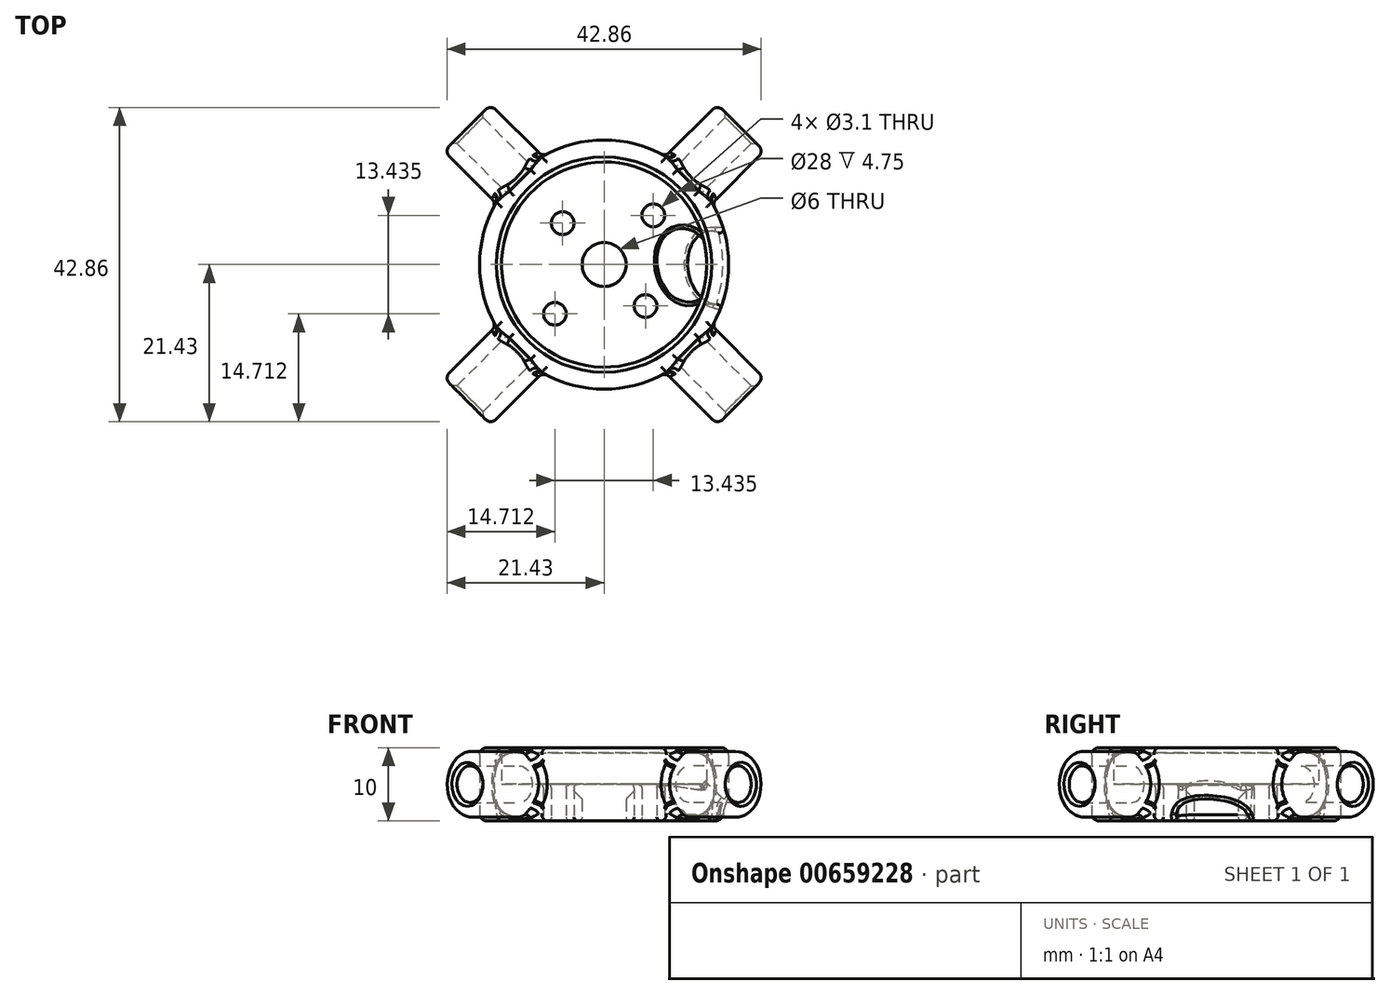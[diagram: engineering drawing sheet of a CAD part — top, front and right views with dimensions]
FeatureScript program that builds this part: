
annotation { "Feature Type Name" : "Feature", "Feature Type Description" : "" }
export const myFeature = defineFeature(function(context is Context, id is Id, definition is map)
    precondition{}
    {
        {
            var Q0;
            Q0=qCreatedBy(makeId("Top.planeOp"),FACE);
            var sketch = newSketch(context, id + "F0", { "sketchPlane" : qUnion([Q0])});
            skCircle(sketch, "E0", {"center": v(0, 0) * mm, "radius": 14 * mm});
            skCircle(sketch, "E1", {"center": v(0, 0) * mm, "radius": 17 * mm});
            skCircle(sketch, "E2", {"center": v(-9.5, 0) * mm, "radius": 1.55 * mm});
            skCircle(sketch, "E3", {"center": v(0, 8) * mm, "radius": 1.55 * mm});
            skCircle(sketch, "E4", {"center": v(9.5, 0) * mm, "radius": 1.55 * mm});
            skCircle(sketch, "E5", {"center": v(0, -8) * mm, "radius": 1.55 * mm});
            skCircle(sketch, "E6", {"center": v(0, 0) * mm, "radius": 3 * mm});
            skLineSegment(sketch, "E7", {"start": v(-16.4, 4.5) * mm, "end": v(-16.4, -4.5) * mm});
            skLineSegment(sketch, "E8", {"start": v(16.4, 4.5) * mm, "end": v(16.4, -4.5) * mm});
            skLineSegment(sketch, "E9", {"start": v(-4.5, 16.4) * mm, "end": v(4.5, 16.4) * mm});
            skLineSegment(sketch, "E10", {"start": v(-4.5, -16.4) * mm, "end": v(4.5, -16.4) * mm});
            skSolve(sketch);
        }
        {
            var Q0;
            Q0=makeQuery(id+"F0.imprint","IMPRINT",FACE,{"disambiguationData":[TD([[makeQuery(id+"F0.imprint","IMPRINT",EDGE,{"derivedFrom":sQuery(id+"F0.wireOp",EDGE,"E0")}),-1.0]])]});
            extrude(context, id + "F1", {"entities" : qUnion([Q0]), "depth" : 10 * mm, "offsetDistance" : 25 * mm});
        }
        {
            var Q0;
            Q0=makeQuery(id+"F0.imprint","IMPRINT",FACE,{"disambiguationData":[TD([[makeQuery(id+"F0.imprint","IMPRINT",EDGE,{"derivedFrom":sQuery(id+"F0.wireOp",EDGE,"E0")}),1.0]])]});
            extrude(context, id + "F2", {"entities" : qUnion([Q0]), "operationType" : NewBodyOperationType.ADD, "depth" : 5 * mm, "offsetDistance" : 25 * mm});
        }
        {
            var Q0;
            Q0=sQuery(id+"F0.wireOp",EDGE,"E7");
            cPlane(context, id + "F3", {"entities" : qUnion([Q0]), "cplaneType" : CPlaneType.LINE_ANGLE, "offset" : 25 * mm, "angle" : 90 * degree, "width" : 150 * mm, "height" : 150 * mm});
        }
        {
            var Q0;
            Q0=qCreatedBy(id+"F3.planeOp",FACE);
            var sketch = newSketch(context, id + "F4", { "sketchPlane" : qUnion([Q0])});
            skCircle(sketch, "E11", {"center": v(0, 5) * mm, "radius": 2.5 * mm});
            skCircle(sketch, "E12", {"center": v(0, 5) * mm, "radius": 4.5 * mm});
            skSolve(sketch);
        }
        {
            var Q0;
            Q0=makeQuery(id+"F4.imprint","IMPRINT",FACE,{"disambiguationData":[TD([[makeQuery(id+"F4.imprint","IMPRINT",EDGE,{"derivedFrom":sQuery(id+"F4.wireOp",EDGE,"E11")}),-1.0]])]});
            extrude(context, id + "F5", {"entities" : qUnion([Q0]), "oppositeDirection" : true, "depth" : 10 * mm, "offsetDistance" : 25 * mm});
        }
        {
            var Q0;
            Q0=sQuery(id+"F0.wireOp",EDGE,"E8");
            cPlane(context, id + "F6", {"entities" : qUnion([Q0]), "cplaneType" : CPlaneType.LINE_ANGLE, "offset" : 25 * mm, "angle" : 90 * degree, "width" : 150 * mm, "height" : 150 * mm});
        }
        {
            var Q0;
            Q0=qCreatedBy(id+"F6.planeOp",FACE);
            var sketch = newSketch(context, id + "F7", { "sketchPlane" : qUnion([Q0])});
            skCircle(sketch, "E13", {"center": v(0, 5) * mm, "radius": 2.5 * mm});
            skCircle(sketch, "E14", {"center": v(0, 5) * mm, "radius": 4.5 * mm});
            skSolve(sketch);
        }
        {
            var Q0;
            Q0=makeQuery(id+"F7.imprint","IMPRINT",FACE,{"disambiguationData":[TD([[makeQuery(id+"F7.imprint","IMPRINT",EDGE,{"derivedFrom":sQuery(id+"F7.wireOp",EDGE,"E13")}),-1.0]])]});
            extrude(context, id + "F8", {"entities" : qUnion([Q0]), "depth" : 10 * mm, "offsetDistance" : 25 * mm});
        }
        {
            var Q0;
            Q0=sQuery(id+"F0.wireOp",EDGE,"E10");
            cPlane(context, id + "F9", {"entities" : qUnion([Q0]), "cplaneType" : CPlaneType.LINE_ANGLE, "offset" : 25 * mm, "angle" : 180 * degree, "width" : 150 * mm, "height" : 150 * mm});
        }
        {
            var Q0;
            Q0=qCreatedBy(id+"F9.planeOp",FACE);
            var sketch = newSketch(context, id + "F10", { "sketchPlane" : qUnion([Q0])});
            skCircle(sketch, "E15", {"center": v(0, 5) * mm, "radius": 2.5 * mm});
            skCircle(sketch, "E16", {"center": v(0, 5) * mm, "radius": 4.5 * mm});
            skSolve(sketch);
        }
        {
            var Q0;
            Q0=makeQuery(id+"F10.imprint","IMPRINT",FACE,{"disambiguationData":[TD([[makeQuery(id+"F10.imprint","IMPRINT",EDGE,{"derivedFrom":sQuery(id+"F10.wireOp",EDGE,"E15")}),-1.0]])]});
            extrude(context, id + "F11", {"entities" : qUnion([Q0]), "depth" : 10 * mm, "offsetDistance" : 25 * mm});
        }
        {
            var Q0;
            Q0=sQuery(id+"F0.wireOp",EDGE,"E9");
            cPlane(context, id + "F12", {"entities" : qUnion([Q0]), "cplaneType" : CPlaneType.LINE_ANGLE, "offset" : 25 * mm, "angle" : 0 * degree, "width" : 150 * mm, "height" : 150 * mm});
        }
        {
            var Q0;
            Q0=qCreatedBy(id+"F12.planeOp",FACE);
            var sketch = newSketch(context, id + "F13", { "sketchPlane" : qUnion([Q0])});
            skCircle(sketch, "E17", {"center": v(0, 5) * mm, "radius": 2.5 * mm});
            skCircle(sketch, "E18", {"center": v(0, 5) * mm, "radius": 4.5 * mm});
            skSolve(sketch);
        }
        {
            var Q0;
            Q0=makeQuery(id+"F13.imprint","IMPRINT",FACE,{"disambiguationData":[TD([[makeQuery(id+"F13.imprint","IMPRINT",EDGE,{"derivedFrom":sQuery(id+"F13.wireOp",EDGE,"E17")}),-1.0]])]});
            extrude(context, id + "F14", {"entities" : qUnion([Q0]), "depth" : 10 * mm, "offsetDistance" : 25 * mm});
        }
        {
            var Q0;
            Q0=makeQuery(id+"F14.opExtrude","SWEPT_BODY",BODY,{"disambiguationData":[OSD([sQuery(id+"F13.wireOp",EDGE,"E17"),sQuery(id+"F13.wireOp",EDGE,"E18")])]});
            var Q1;
            Q1=makeQuery(id+"F1.opExtrude","SWEPT_BODY",BODY,{"disambiguationData":[OSD([sQuery(id+"F0.wireOp",EDGE,"E0"),sQuery(id+"F0.wireOp",EDGE,"E1"),sQuery(id+"F0.wireOp",EDGE,"E7"),sQuery(id+"F0.wireOp",EDGE,"E8"),sQuery(id+"F0.wireOp",EDGE,"E9"),sQuery(id+"F0.wireOp",EDGE,"E10")])]});
            var Q2;
            Q2=makeQuery(id+"F5.opExtrude","SWEPT_BODY",BODY,{"disambiguationData":[OSD([sQuery(id+"F4.wireOp",EDGE,"E11"),sQuery(id+"F4.wireOp",EDGE,"E12")])]});
            var Q3;
            Q3=makeQuery(id+"F11.opExtrude","SWEPT_BODY",BODY,{"disambiguationData":[OSD([sQuery(id+"F10.wireOp",EDGE,"E15"),sQuery(id+"F10.wireOp",EDGE,"E16")])]});
            var Q4;
            Q4=makeQuery(id+"F8.opExtrude","SWEPT_BODY",BODY,{"disambiguationData":[OSD([sQuery(id+"F7.wireOp",EDGE,"E13"),sQuery(id+"F7.wireOp",EDGE,"E14")])]});
            booleanBodies(context, id + "F15", {"operationType" : BooleanOperationType.UNION, "tools" : qUnion([Q0, Q1, Q2, Q3, Q4])});
        }
        {
            var Q0;
            {var subQ1=sQuery(id+"F0.wireOp",EDGE,"E8");var subQ2=sQuery(id+"F0.wireOp",EDGE,"E1");Q0=makeQuery(id+"F15.opBoolean","SPLIT",EDGE,{"disambiguationData":[TD([makeQuery(id+"F1.opExtrude","SWEPT_FACE",FACE,{"disambiguationData":[OSD([subQ2]),TDD([makeQuery(id+"F0.imprint","IMPRINT",EDGE,{"disambiguationData":[TD([[makeQuery(id+"F0.imprint","INTERSECT",VERTEX,{"disambiguationData":[OD(0.0)],"derivedFrom":[subQ2,subQ1]}),-1.0]])],"derivedFrom":subQ2})])]})])],"derivedFrom":makeQuery(id+"F1.opExtrude","CAP_EDGE",EDGE,{"disambiguationData":[OSD([subQ1])],"isStart":true})});}
            var Q1;
            {var subQ1=sQuery(id+"F0.wireOp",EDGE,"E8");var subQ2=sQuery(id+"F0.wireOp",EDGE,"E1");Q1=makeQuery(id+"F15.opBoolean","SPLIT",EDGE,{"disambiguationData":[TD([makeQuery(id+"F1.opExtrude","SWEPT_FACE",FACE,{"disambiguationData":[OSD([subQ2]),TDD([makeQuery(id+"F0.imprint","IMPRINT",EDGE,{"disambiguationData":[TD([[makeQuery(id+"F0.imprint","INTERSECT",VERTEX,{"disambiguationData":[OD(1.0)],"derivedFrom":[subQ2,subQ1]}),1.0]])],"derivedFrom":subQ2})])]})])],"derivedFrom":makeQuery(id+"F1.opExtrude","CAP_EDGE",EDGE,{"disambiguationData":[OSD([subQ1])],"isStart":true})});}
            var Q2;
            {var subQ1=sQuery(id+"F0.wireOp",EDGE,"E10");var subQ2=sQuery(id+"F0.wireOp",EDGE,"E8");var subQ3=sQuery(id+"F0.wireOp",EDGE,"E1");Q2=makeQuery(id+"F15.opBoolean","SPLIT",EDGE,{"disambiguationData":[TD([makeQuery(id+"F1.opExtrude","SWEPT_FACE",FACE,{"disambiguationData":[OSD([subQ3]),TDD([makeQuery(id+"F0.imprint","IMPRINT",EDGE,{"disambiguationData":[TD([[makeQuery(id+"F0.imprint","INTERSECT",VERTEX,{"disambiguationData":[OD(1.0)],"derivedFrom":[subQ3,subQ2]}),1.0]])],"derivedFrom":subQ3})])]})])],"derivedFrom":makeQuery(id+"F1.opExtrude","CAP_EDGE",EDGE,{"disambiguationData":[OSD([subQ1])],"isStart":true})});}
            var Q3;
            {var subQ1=sQuery(id+"F0.wireOp",EDGE,"E7");var subQ2=sQuery(id+"F0.wireOp",EDGE,"E1");var subQ3=sQuery(id+"F0.wireOp",EDGE,"E10");Q3=makeQuery(id+"F15.opBoolean","SPLIT",EDGE,{"disambiguationData":[TD([makeQuery(id+"F1.opExtrude","SWEPT_FACE",FACE,{"disambiguationData":[OSD([subQ2]),TDD([makeQuery(id+"F0.imprint","IMPRINT",EDGE,{"disambiguationData":[TD([[makeQuery(id+"F0.imprint","INTERSECT",VERTEX,{"disambiguationData":[OD(1.0)],"derivedFrom":[subQ2,subQ1]}),-1.0]])],"derivedFrom":subQ2})])]})])],"derivedFrom":makeQuery(id+"F1.opExtrude","CAP_EDGE",EDGE,{"disambiguationData":[OSD([subQ3])],"isStart":true})});}
            var Q4;
            {var subQ1=sQuery(id+"F0.wireOp",EDGE,"E7");var subQ2=sQuery(id+"F0.wireOp",EDGE,"E1");Q4=makeQuery(id+"F15.opBoolean","SPLIT",EDGE,{"disambiguationData":[TD([makeQuery(id+"F1.opExtrude","SWEPT_FACE",FACE,{"disambiguationData":[OSD([subQ2]),TDD([makeQuery(id+"F0.imprint","IMPRINT",EDGE,{"disambiguationData":[TD([[makeQuery(id+"F0.imprint","INTERSECT",VERTEX,{"disambiguationData":[OD(1.0)],"derivedFrom":[subQ2,subQ1]}),-1.0]])],"derivedFrom":subQ2})])]})])],"derivedFrom":makeQuery(id+"F1.opExtrude","CAP_EDGE",EDGE,{"disambiguationData":[OSD([subQ1])],"isStart":true})});}
            var Q5;
            {var subQ1=sQuery(id+"F0.wireOp",EDGE,"E7");var subQ2=sQuery(id+"F0.wireOp",EDGE,"E1");Q5=makeQuery(id+"F15.opBoolean","SPLIT",EDGE,{"disambiguationData":[TD([makeQuery(id+"F1.opExtrude","SWEPT_FACE",FACE,{"disambiguationData":[OSD([subQ2]),TDD([makeQuery(id+"F0.imprint","IMPRINT",EDGE,{"disambiguationData":[TD([[makeQuery(id+"F0.imprint","INTERSECT",VERTEX,{"disambiguationData":[OD(0.0)],"derivedFrom":[subQ2,subQ1]}),1.0]])],"derivedFrom":subQ2})])]})])],"derivedFrom":makeQuery(id+"F1.opExtrude","CAP_EDGE",EDGE,{"disambiguationData":[OSD([subQ1])],"isStart":true})});}
            var Q6;
            {var subQ1=sQuery(id+"F0.wireOp",EDGE,"E9");var subQ2=sQuery(id+"F0.wireOp",EDGE,"E7");var subQ3=sQuery(id+"F0.wireOp",EDGE,"E1");Q6=makeQuery(id+"F15.opBoolean","SPLIT",EDGE,{"disambiguationData":[TD([makeQuery(id+"F1.opExtrude","SWEPT_FACE",FACE,{"disambiguationData":[OSD([subQ3]),TDD([makeQuery(id+"F0.imprint","IMPRINT",EDGE,{"disambiguationData":[TD([[makeQuery(id+"F0.imprint","INTERSECT",VERTEX,{"disambiguationData":[OD(0.0)],"derivedFrom":[subQ3,subQ2]}),1.0]])],"derivedFrom":subQ3})])]})])],"derivedFrom":makeQuery(id+"F1.opExtrude","CAP_EDGE",EDGE,{"disambiguationData":[OSD([subQ1])],"isStart":true})});}
            var Q7;
            {var subQ1=sQuery(id+"F0.wireOp",EDGE,"E9");var subQ2=sQuery(id+"F0.wireOp",EDGE,"E8");var subQ3=sQuery(id+"F0.wireOp",EDGE,"E1");Q7=makeQuery(id+"F15.opBoolean","SPLIT",EDGE,{"disambiguationData":[TD([makeQuery(id+"F1.opExtrude","SWEPT_FACE",FACE,{"disambiguationData":[OSD([subQ3]),TDD([makeQuery(id+"F0.imprint","IMPRINT",EDGE,{"disambiguationData":[TD([[makeQuery(id+"F0.imprint","INTERSECT",VERTEX,{"disambiguationData":[OD(0.0)],"derivedFrom":[subQ3,subQ2]}),-1.0]])],"derivedFrom":subQ3})])]})])],"derivedFrom":makeQuery(id+"F1.opExtrude","CAP_EDGE",EDGE,{"disambiguationData":[OSD([subQ1])],"isStart":true})});}
            fillet(context, id + "F16", {"entities" : qUnion([Q0, Q1, Q2, Q3, Q4, Q5, Q6, Q7]), "radius" : 1 * mm, "tangentPropagation" : true, "allowEdgeOverflow" : false});
        }
        {
            var Q0;
            {var subQ1=sQuery(id+"F0.wireOp",EDGE,"E7");var subQ2=sQuery(id+"F0.wireOp",EDGE,"E1");Q0=makeQuery(id+"F15.opBoolean","SPLIT",EDGE,{"disambiguationData":[TD([makeQuery(id+"F1.opExtrude","SWEPT_FACE",FACE,{"disambiguationData":[OSD([subQ2]),TDD([makeQuery(id+"F0.imprint","IMPRINT",EDGE,{"disambiguationData":[TD([[makeQuery(id+"F0.imprint","INTERSECT",VERTEX,{"disambiguationData":[OD(0.0)],"derivedFrom":[subQ2,subQ1]}),1.0]])],"derivedFrom":subQ2})])]})])],"derivedFrom":makeQuery(id+"F1.opExtrude","CAP_EDGE",EDGE,{"disambiguationData":[OSD([subQ1])],"isStart":false})});}
            var Q1;
            {var subQ1=sQuery(id+"F0.wireOp",EDGE,"E7");var subQ2=sQuery(id+"F0.wireOp",EDGE,"E1");Q1=makeQuery(id+"F15.opBoolean","SPLIT",EDGE,{"disambiguationData":[TD([makeQuery(id+"F1.opExtrude","SWEPT_FACE",FACE,{"disambiguationData":[OSD([subQ2]),TDD([makeQuery(id+"F0.imprint","IMPRINT",EDGE,{"disambiguationData":[TD([[makeQuery(id+"F0.imprint","INTERSECT",VERTEX,{"disambiguationData":[OD(1.0)],"derivedFrom":[subQ2,subQ1]}),-1.0]])],"derivedFrom":subQ2})])]})])],"derivedFrom":makeQuery(id+"F1.opExtrude","CAP_EDGE",EDGE,{"disambiguationData":[OSD([subQ1])],"isStart":false})});}
            var Q2;
            {var subQ0=sQuery(id+"F0.wireOp",EDGE,"E10");var subQ1=sQuery(id+"F0.wireOp",EDGE,"E7");var subQ2=sQuery(id+"F0.wireOp",EDGE,"E1");Q2=makeQuery(id+"F15.opBoolean","SPLIT",EDGE,{"disambiguationData":[TD([makeQuery(id+"F1.opExtrude","SWEPT_FACE",FACE,{"disambiguationData":[OSD([subQ2]),TDD([makeQuery(id+"F0.imprint","IMPRINT",EDGE,{"disambiguationData":[TD([[makeQuery(id+"F0.imprint","INTERSECT",VERTEX,{"disambiguationData":[OD(1.0)],"derivedFrom":[subQ2,subQ1]}),-1.0]])],"derivedFrom":subQ2})])]})])],"derivedFrom":makeQuery(id+"F1.opExtrude","CAP_EDGE",EDGE,{"disambiguationData":[OSD([subQ0])],"isStart":false})});}
            var Q3;
            {var subQ0=sQuery(id+"F0.wireOp",EDGE,"E10");var subQ1=sQuery(id+"F0.wireOp",EDGE,"E8");var subQ2=sQuery(id+"F0.wireOp",EDGE,"E1");Q3=makeQuery(id+"F15.opBoolean","SPLIT",EDGE,{"disambiguationData":[TD([makeQuery(id+"F1.opExtrude","SWEPT_FACE",FACE,{"disambiguationData":[OSD([subQ2]),TDD([makeQuery(id+"F0.imprint","IMPRINT",EDGE,{"disambiguationData":[TD([[makeQuery(id+"F0.imprint","INTERSECT",VERTEX,{"disambiguationData":[OD(1.0)],"derivedFrom":[subQ2,subQ1]}),1.0]])],"derivedFrom":subQ2})])]})])],"derivedFrom":makeQuery(id+"F1.opExtrude","CAP_EDGE",EDGE,{"disambiguationData":[OSD([subQ0])],"isStart":false})});}
            var Q4;
            {var subQ1=sQuery(id+"F0.wireOp",EDGE,"E8");var subQ2=sQuery(id+"F0.wireOp",EDGE,"E1");Q4=makeQuery(id+"F15.opBoolean","SPLIT",EDGE,{"disambiguationData":[TD([makeQuery(id+"F1.opExtrude","SWEPT_FACE",FACE,{"disambiguationData":[OSD([subQ2]),TDD([makeQuery(id+"F0.imprint","IMPRINT",EDGE,{"disambiguationData":[TD([[makeQuery(id+"F0.imprint","INTERSECT",VERTEX,{"disambiguationData":[OD(1.0)],"derivedFrom":[subQ2,subQ1]}),1.0]])],"derivedFrom":subQ2})])]})])],"derivedFrom":makeQuery(id+"F1.opExtrude","CAP_EDGE",EDGE,{"disambiguationData":[OSD([subQ1])],"isStart":false})});}
            var Q5;
            {var subQ1=sQuery(id+"F0.wireOp",EDGE,"E8");var subQ2=sQuery(id+"F0.wireOp",EDGE,"E1");Q5=makeQuery(id+"F15.opBoolean","SPLIT",EDGE,{"disambiguationData":[TD([makeQuery(id+"F1.opExtrude","SWEPT_FACE",FACE,{"disambiguationData":[OSD([subQ2]),TDD([makeQuery(id+"F0.imprint","IMPRINT",EDGE,{"disambiguationData":[TD([[makeQuery(id+"F0.imprint","INTERSECT",VERTEX,{"disambiguationData":[OD(0.0)],"derivedFrom":[subQ2,subQ1]}),-1.0]])],"derivedFrom":subQ2})])]})])],"derivedFrom":makeQuery(id+"F1.opExtrude","CAP_EDGE",EDGE,{"disambiguationData":[OSD([subQ1])],"isStart":false})});}
            var Q6;
            {var subQ0=sQuery(id+"F0.wireOp",EDGE,"E9");var subQ1=sQuery(id+"F0.wireOp",EDGE,"E8");var subQ2=sQuery(id+"F0.wireOp",EDGE,"E1");Q6=makeQuery(id+"F15.opBoolean","SPLIT",EDGE,{"disambiguationData":[TD([makeQuery(id+"F1.opExtrude","SWEPT_FACE",FACE,{"disambiguationData":[OSD([subQ2]),TDD([makeQuery(id+"F0.imprint","IMPRINT",EDGE,{"disambiguationData":[TD([[makeQuery(id+"F0.imprint","INTERSECT",VERTEX,{"disambiguationData":[OD(0.0)],"derivedFrom":[subQ2,subQ1]}),-1.0]])],"derivedFrom":subQ2})])]})])],"derivedFrom":makeQuery(id+"F1.opExtrude","CAP_EDGE",EDGE,{"disambiguationData":[OSD([subQ0])],"isStart":false})});}
            var Q7;
            {var subQ0=sQuery(id+"F0.wireOp",EDGE,"E9");var subQ1=sQuery(id+"F0.wireOp",EDGE,"E7");var subQ2=sQuery(id+"F0.wireOp",EDGE,"E1");Q7=makeQuery(id+"F15.opBoolean","SPLIT",EDGE,{"disambiguationData":[TD([makeQuery(id+"F1.opExtrude","SWEPT_FACE",FACE,{"disambiguationData":[OSD([subQ2]),TDD([makeQuery(id+"F0.imprint","IMPRINT",EDGE,{"disambiguationData":[TD([[makeQuery(id+"F0.imprint","INTERSECT",VERTEX,{"disambiguationData":[OD(0.0)],"derivedFrom":[subQ2,subQ1]}),1.0]])],"derivedFrom":subQ2})])]})])],"derivedFrom":makeQuery(id+"F1.opExtrude","CAP_EDGE",EDGE,{"disambiguationData":[OSD([subQ0])],"isStart":false})});}
            fillet(context, id + "F17", {"entities" : qUnion([Q0, Q1, Q2, Q3, Q4, Q5, Q6, Q7]), "radius" : 1 * mm, "tangentPropagation" : true, "allowEdgeOverflow" : false});
        }
        {
            var Q0;
            Q0=makeQuery(id+"F11.opExtrude","SWEPT_FACE",FACE,{"disambiguationData":[OSD([sQuery(id+"F10.wireOp",EDGE,"E16")])]});
            var Q1;
            Q1=makeQuery(id+"F5.opExtrude","SWEPT_FACE",FACE,{"disambiguationData":[OSD([sQuery(id+"F4.wireOp",EDGE,"E12")])]});
            var Q2;
            Q2=makeQuery(id+"F14.opExtrude","SWEPT_FACE",FACE,{"disambiguationData":[OSD([sQuery(id+"F13.wireOp",EDGE,"E18")])]});
            var Q3;
            Q3=makeQuery(id+"F8.opExtrude","SWEPT_FACE",FACE,{"disambiguationData":[OSD([sQuery(id+"F7.wireOp",EDGE,"E14")])]});
            fillet(context, id + "F18", {"entities" : qUnion([Q0, Q1, Q2, Q3]), "radius" : 1 * mm, "tangentPropagation" : true, "allowEdgeOverflow" : false});
        }
        {
            var Q0;
            {var subQ0=sQuery(id+"F0.wireOp",EDGE,"E1");Q0=makeQuery(id+"F1.opExtrude","SWEPT_FACE",FACE,{"disambiguationData":[OSD([subQ0]),TDD([makeQuery(id+"F0.imprint","IMPRINT",EDGE,{"disambiguationData":[TD([[makeQuery(id+"F0.imprint","INTERSECT",VERTEX,{"disambiguationData":[OD(1.0)],"derivedFrom":[subQ0,sQuery(id+"F0.wireOp",EDGE,"E8")]}),1.0]])],"derivedFrom":subQ0})])]});}
            var Q1;
            {var subQ0=sQuery(id+"F0.wireOp",EDGE,"E1");Q1=makeQuery(id+"F1.opExtrude","SWEPT_FACE",FACE,{"disambiguationData":[OSD([subQ0]),TDD([makeQuery(id+"F0.imprint","IMPRINT",EDGE,{"disambiguationData":[TD([[makeQuery(id+"F0.imprint","INTERSECT",VERTEX,{"disambiguationData":[OD(0.0)],"derivedFrom":[subQ0,sQuery(id+"F0.wireOp",EDGE,"E8")]}),-1.0]])],"derivedFrom":subQ0})])]});}
            var Q2;
            {var subQ0=sQuery(id+"F0.wireOp",EDGE,"E1");Q2=makeQuery(id+"F1.opExtrude","SWEPT_FACE",FACE,{"disambiguationData":[OSD([subQ0]),TDD([makeQuery(id+"F0.imprint","IMPRINT",EDGE,{"disambiguationData":[TD([[makeQuery(id+"F0.imprint","INTERSECT",VERTEX,{"disambiguationData":[OD(0.0)],"derivedFrom":[subQ0,sQuery(id+"F0.wireOp",EDGE,"E7")]}),1.0]])],"derivedFrom":subQ0})])]});}
            var Q3;
            {var subQ0=sQuery(id+"F0.wireOp",EDGE,"E1");Q3=makeQuery(id+"F1.opExtrude","SWEPT_FACE",FACE,{"disambiguationData":[OSD([subQ0]),TDD([makeQuery(id+"F0.imprint","IMPRINT",EDGE,{"disambiguationData":[TD([[makeQuery(id+"F0.imprint","INTERSECT",VERTEX,{"disambiguationData":[OD(1.0)],"derivedFrom":[subQ0,sQuery(id+"F0.wireOp",EDGE,"E7")]}),-1.0]])],"derivedFrom":subQ0})])]});}
            fillet(context, id + "F19", {"entities" : qUnion([Q0, Q1, Q2, Q3]), "radius" : 1 * mm, "tangentPropagation" : true, "allowEdgeOverflow" : false});
        }
        {
            var Q0;
            Q0=makeQuery(id+"F2.opExtrude","CAP_EDGE",EDGE,{"disambiguationData":[OSD([sQuery(id+"F0.wireOp",EDGE,"E6")])],"isStart":false});
            chamfer(context, id + "F20", {"entities" : qUnion([Q0]), "width" : 2 * mm, "tangentPropagation" : true});
        }
        {
            var Q0;
            Q0=makeQuery(id+"F1.opExtrude","CAP_EDGE",EDGE,{"disambiguationData":[OSD([sQuery(id+"F0.wireOp",EDGE,"E0")])],"isStart":false});
            chamfer(context, id + "F21", {"entities" : qUnion([Q0]), "width" : .7 * mm, "tangentPropagation" : true});
        }
        {
            var Q0;
            Q0=makeQuery(id+"F14.opExtrude","CAP_EDGE",EDGE,{"disambiguationData":[OSD([sQuery(id+"F13.wireOp",EDGE,"E17")])],"isStart":false});
            var Q1;
            Q1=makeQuery(id+"F5.opExtrude","CAP_EDGE",EDGE,{"disambiguationData":[OSD([sQuery(id+"F4.wireOp",EDGE,"E11")])],"isStart":false});
            var Q2;
            Q2=makeQuery(id+"F11.opExtrude","CAP_EDGE",EDGE,{"disambiguationData":[OSD([sQuery(id+"F10.wireOp",EDGE,"E15")])],"isStart":false});
            var Q3;
            Q3=makeQuery(id+"F8.opExtrude","CAP_EDGE",EDGE,{"disambiguationData":[OSD([sQuery(id+"F7.wireOp",EDGE,"E13")])],"isStart":false});
            chamfer(context, id + "F22", {"entities" : qUnion([Q0, Q1, Q2, Q3]), "width" : .5 * mm, "tangentPropagation" : true});
        }
        {
            var Q0;
            {var subQ0=sQuery(id+"F0.wireOp",EDGE,"E10");var subQ1=sQuery(id+"F0.wireOp",EDGE,"E8");var subQ2=sQuery(id+"F0.wireOp",EDGE,"E1");Q0=makeQuery(id+"F19.opFillet","BLEND_EDGE",EDGE,{"blendedFrom":[makeQuery(id+"F1.opExtrude","CAP_EDGE",EDGE,{"disambiguationData":[OSD([subQ2]),TDD([makeQuery(id+"F0.imprint","IMPRINT",EDGE,{"disambiguationData":[TD([[makeQuery(id+"F0.imprint","INTERSECT",VERTEX,{"disambiguationData":[OD(1.0)],"derivedFrom":[subQ2,subQ1]}),1.0]])],"derivedFrom":subQ2})])],"isStart":false}),makeQuery(id+"F1.opExtrude","CAP_FACE",FACE,{"disambiguationData":[OSD([sQuery(id+"F0.wireOp",EDGE,"E0"),subQ2,sQuery(id+"F0.wireOp",EDGE,"E7"),subQ1,sQuery(id+"F0.wireOp",EDGE,"E9"),subQ0])],"isStart":false})],"blendedInto":[makeQuery(id+"F1.opExtrude","CAP_FACE",FACE,{"disambiguationData":[OSD([sQuery(id+"F0.wireOp",EDGE,"E0"),subQ2,sQuery(id+"F0.wireOp",EDGE,"E7"),subQ1,sQuery(id+"F0.wireOp",EDGE,"E9"),subQ0])],"isStart":false})]});}
            cPoint(context, id + "F23", {"entities" : qUnion([Q0]), "parameter" : 0.5});
        }
        {
            var Q0;
            Q0=sQuery(id+"F0.wireOp",VERTEX,"E5.center");
            var Q1;
            Q1 = qCreatedBy(id + "F23" ,VERTEX);
            var Q2;
            Q2=sQuery(id+"F0.wireOp",VERTEX,"E4.center");
            cPlane(context, id + "F24", {"entities" : qUnion([Q0, Q1, Q2]), "cplaneType" : CPlaneType.THREE_POINT, "offset" : 25 * mm, "width" : 150 * mm, "height" : 150 * mm});
        }
        {
            var Q0;
            Q0=qCreatedBy(id+"F24.planeOp",FACE);
            var sketch = newSketch(context, id + "F25", { "sketchPlane" : qUnion([Q0])});
            skEllipse(sketch, "E19", {"center": v(6.32, 9.04) * mm, "majorRadius": 5 * mm, "minorRadius": 2.5 * mm, "majorAxis": v(-0.8, 0.6)});
            skSolve(sketch);
        }
        {
            var Q0;
            Q0 = qSketchRegion(id + "F25", true);
            extrude(context, id + "F26", {"entities" : qUnion([Q0]), "operationType" : NewBodyOperationType.REMOVE, "depth" : 25 * mm, "offsetDistance" : 25 * mm, "symmetric" : true});
        }
        {
            var Q0;
            Q0=makeQuery(id+"F26.boolean.opBoolean","COPY",FACE,{"derivedFrom":makeQuery(id+"F26.opExtrude","SWEPT_FACE",FACE,{"disambiguationData":[OSD([sQuery(id+"F25.wireOp",EDGE,"E19")])]})});
            var Q1;
            Q1=makeQuery(id+"F20.opChamfer","BLEND_FACE",FACE,{"disambiguationData":[OSD([sQuery(id+"F0.wireOp",EDGE,"E6")])]});
            var Q2;
            Q2=makeQuery(id+"F2.opExtrude","CAP_EDGE",EDGE,{"disambiguationData":[OSD([sQuery(id+"F0.wireOp",EDGE,"E6")])],"isStart":true});
            var Q3;
            Q3=makeQuery(id+"F2.opExtrude","CAP_EDGE",EDGE,{"disambiguationData":[OSD([sQuery(id+"F0.wireOp",EDGE,"E5")])],"isStart":false});
            var Q4;
            Q4=makeQuery(id+"F2.opExtrude","CAP_EDGE",EDGE,{"disambiguationData":[OSD([sQuery(id+"F0.wireOp",EDGE,"E2")])],"isStart":false});
            var Q5;
            Q5=makeQuery(id+"F2.opExtrude","CAP_EDGE",EDGE,{"disambiguationData":[OSD([sQuery(id+"F0.wireOp",EDGE,"E3")])],"isStart":false});
            var Q6;
            Q6=makeQuery(id+"F2.opExtrude","CAP_EDGE",EDGE,{"disambiguationData":[OSD([sQuery(id+"F0.wireOp",EDGE,"E4")])],"isStart":false});
            var Q7;
            Q7=makeQuery(id+"F2.opExtrude","CAP_EDGE",EDGE,{"disambiguationData":[OSD([sQuery(id+"F0.wireOp",EDGE,"E4")])],"isStart":true});
            var Q8;
            Q8=makeQuery(id+"F2.opExtrude","CAP_EDGE",EDGE,{"disambiguationData":[OSD([sQuery(id+"F0.wireOp",EDGE,"E5")])],"isStart":true});
            var Q9;
            Q9=makeQuery(id+"F2.opExtrude","CAP_EDGE",EDGE,{"disambiguationData":[OSD([sQuery(id+"F0.wireOp",EDGE,"E3")])],"isStart":true});
            var Q10;
            Q10=makeQuery(id+"F2.opExtrude","CAP_EDGE",EDGE,{"disambiguationData":[OSD([sQuery(id+"F0.wireOp",EDGE,"E2")])],"isStart":true});
            fillet(context, id + "F27", {"entities" : qUnion([Q0, Q1, Q2, Q3, Q4, Q5, Q6, Q7, Q8, Q9, Q10]), "radius" : .5 * mm, "tangentPropagation" : true, "allowEdgeOverflow" : false});
        }
        {
            var Q0;
            Q0=makeQuery(id+"F14.opExtrude","SWEPT_BODY",BODY,{"disambiguationData":[OSD([sQuery(id+"F13.wireOp",EDGE,"E17"),sQuery(id+"F13.wireOp",EDGE,"E18")])]});
            var Q1;
            {var subQ0=sQuery(id+"F0.wireOp",EDGE,"E0");Q1=makeQuery(id+"F21.opChamfer","BLEND_EDGE",EDGE,{"blendedFrom":[makeQuery(id+"F1.opExtrude","CAP_EDGE",EDGE,{"disambiguationData":[OSD([subQ0])],"isStart":false}),makeQuery(id+"F1.opExtrude","CAP_FACE",FACE,{"disambiguationData":[OSD([subQ0,sQuery(id+"F0.wireOp",EDGE,"E1"),sQuery(id+"F0.wireOp",EDGE,"E7"),sQuery(id+"F0.wireOp",EDGE,"E8"),sQuery(id+"F0.wireOp",EDGE,"E9"),sQuery(id+"F0.wireOp",EDGE,"E10")])],"isStart":false})],"blendedInto":[makeQuery(id+"F1.opExtrude","CAP_FACE",FACE,{"disambiguationData":[OSD([subQ0,sQuery(id+"F0.wireOp",EDGE,"E1"),sQuery(id+"F0.wireOp",EDGE,"E7"),sQuery(id+"F0.wireOp",EDGE,"E8"),sQuery(id+"F0.wireOp",EDGE,"E9"),sQuery(id+"F0.wireOp",EDGE,"E10")])],"isStart":false})]});}
            transform(context, id + "F28", {"entities" : qUnion([Q0]), "transformType" : TransformType.ROTATION, "transformAxis" : qUnion([Q1]), "angle" : 45 * degree, "makeCopy" : false});
        }
    });
